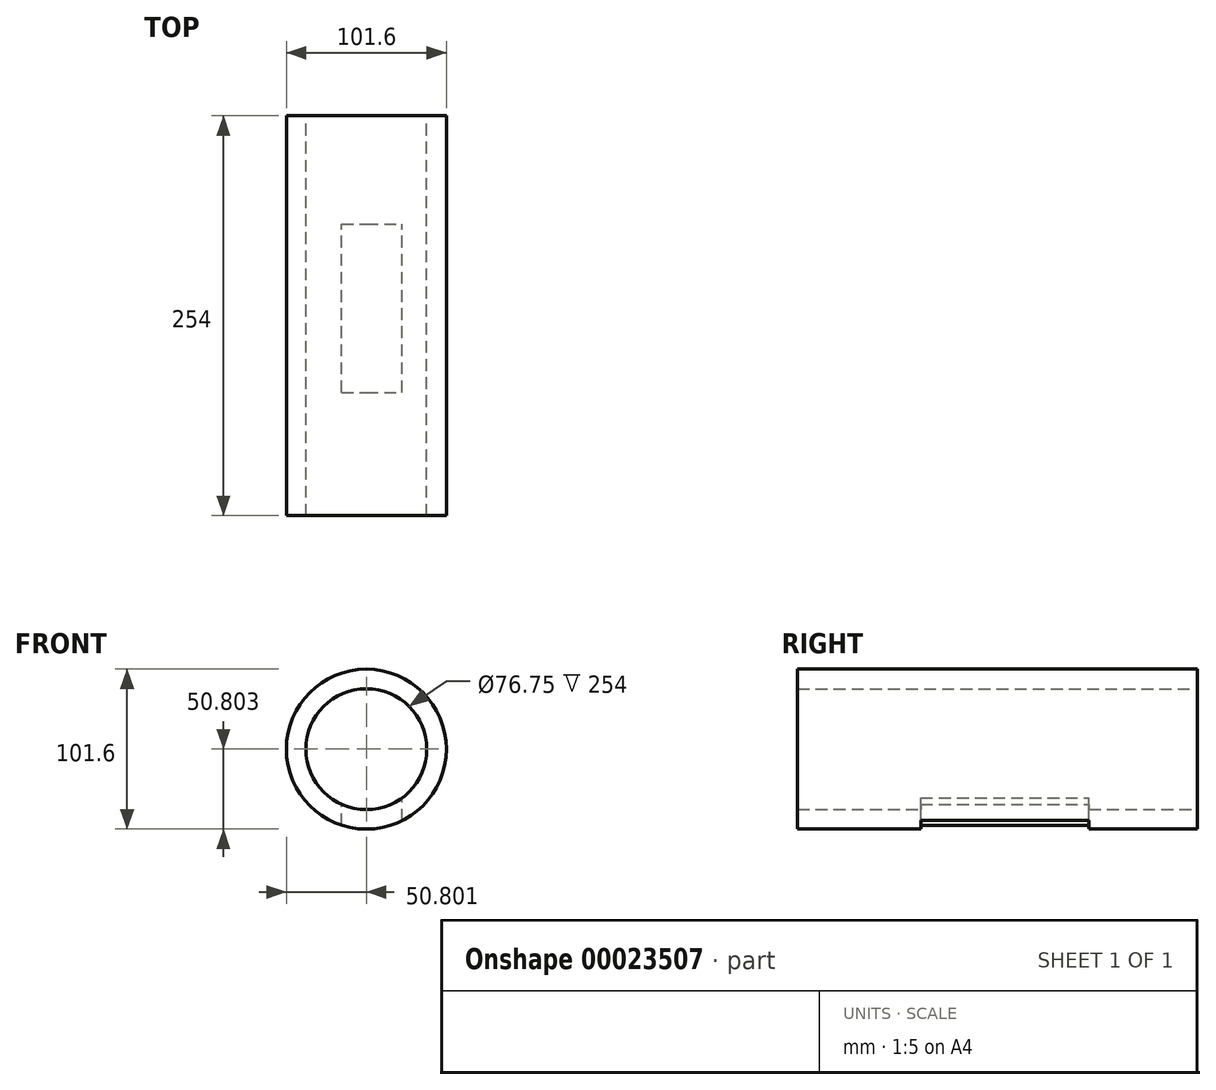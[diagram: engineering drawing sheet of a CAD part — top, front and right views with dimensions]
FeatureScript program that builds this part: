
annotation { "Feature Type Name" : "Feature", "Feature Type Description" : "" }
export const myFeature = defineFeature(function(context is Context, id is Id, definition is map)
    precondition{}
    {
        {
            var Q0;
            Q0=qCreatedBy(makeId("Front.planeOp"),FACE);
            var sketch = newSketch(context, id + "F0", { "sketchPlane" : qUnion([Q0])});
            skCircle(sketch, "E0", {"center": v(-41.6, -9.8) * mm, "radius": 50.8 * mm});
            skCircle(sketch, "E1", {"center": v(-41.6, -9.8) * mm, "radius": 38.37 * mm});
            skSolve(sketch);
        }
        {
            var Q0;
            Q0=makeQuery(id+"F0.imprint","IMPRINT",FACE,{"disambiguationData":[TD([[makeQuery(id+"F0.imprint","IMPRINT",EDGE,{"derivedFrom":sQuery(id+"F0.wireOp",EDGE,"E0")}),1.0]])]});
            extrude(context, id + "F1", {"entities" : qUnion([Q0]), "depth" : 254 * mm});
        }
        {
            var Q0;
            Q0=qCreatedBy(makeId("Top.planeOp"),FACE);
            var sketch = newSketch(context, id + "F2", { "sketchPlane" : qUnion([Q0])});
            skLineSegment(sketch, "E2.bottom", {"start": v(-57.35, -68.84) * mm, "end": v(-18.83, -68.84) * mm});
            skLineSegment(sketch, "E2.top", {"start": v(-57.35, -175.68) * mm, "end": v(-18.83, -175.68) * mm});
            skLineSegment(sketch, "E2.left", {"start": v(-57.35, -68.84) * mm, "end": v(-57.35, -175.68) * mm});
            skLineSegment(sketch, "E2.right", {"start": v(-18.83, -68.84) * mm, "end": v(-18.83, -175.68) * mm});
            skSolve(sketch);
        }
        {
            var Q0;
            Q0=makeQuery(id+"F2.imprint","IMPRINT",FACE,{"disambiguationData":[TD([[makeQuery(id+"F2.imprint","IMPRINT",EDGE,{"derivedFrom":sQuery(id+"F2.wireOp",EDGE,"E2.bottom")}),-1.0]])]});
            extrude(context, id + "F3", {"entities" : qUnion([Q0]), "operationType" : NewBodyOperationType.REMOVE, "oppositeDirection" : true, "depth" : 127 * mm});
        }
    });
